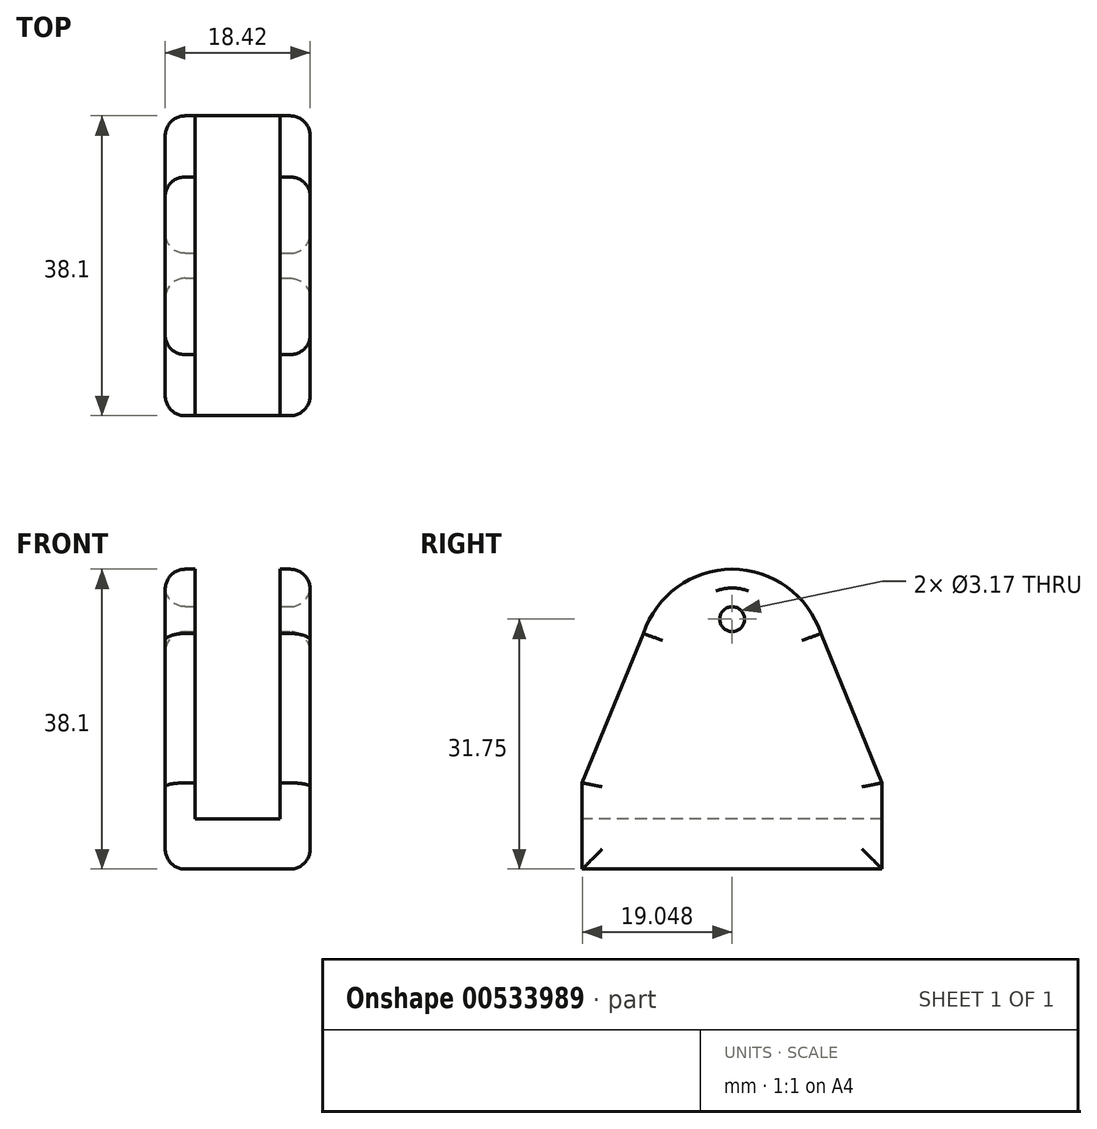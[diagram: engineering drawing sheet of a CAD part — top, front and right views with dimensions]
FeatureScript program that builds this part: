
annotation { "Feature Type Name" : "Feature", "Feature Type Description" : "" }
export const myFeature = defineFeature(function(context is Context, id is Id, definition is map)
    precondition{}
    {
        {
            var Q0;
            Q0=qCreatedBy(makeId("Top.planeOp"),FACE);
            var sketch = newSketch(context, id + "F0", { "sketchPlane" : qUnion([Q0])});
            skLineSegment(sketch, "E0.bottom", {"start": v(0, -20.8) * mm, "end": v(-18.41, -20.8) * mm});
            skLineSegment(sketch, "E0.top", {"start": v(0, -58.9) * mm, "end": v(-18.41, -58.9) * mm});
            skLineSegment(sketch, "E0.left", {"start": v(0, -20.8) * mm, "end": v(0, -58.9) * mm});
            skLineSegment(sketch, "E0.right", {"start": v(-18.42, -20.8) * mm, "end": v(-18.41, -58.9) * mm});
            skSolve(sketch);
        }
        {
            var Q0;
            Q0=makeQuery(id+"F0.imprint","IMPRINT",FACE,{"disambiguationData":[TD([[makeQuery(id+"F0.imprint","IMPRINT",EDGE,{"derivedFrom":sQuery(id+"F0.wireOp",EDGE,"E0.bottom")}),1.0]])]});
            extrude(context, id + "F1", {"entities" : qUnion([Q0]), "depth" : 38.1 * mm, "offsetDistance" : 25.4 * mm});
        }
        {
            var Q0;
            Q0=makeQuery(id+"F1.opExtrude","SWEPT_FACE",FACE,{"disambiguationData":[OSD([sQuery(id+"F0.wireOp",EDGE,"E0.left")])]});
            var sketch = newSketch(context, id + "F2", { "sketchPlane" : qUnion([Q0])});
            skPoint(sketch, "E1.oppositeSnap0", {"position": v(-39.85, 38.1) * mm});
            skLineSegment(sketch, "E1.bottom", {"start": v(-58.9, 0) * mm, "end": v(-39.85, 0) * mm});
            skLineSegment(sketch, "E1.top", {"start": v(-58.9, 31.75) * mm, "end": v(-39.85, 31.75) * mm});
            skLineSegment(sketch, "E1.left", {"start": v(-58.9, 0) * mm, "end": v(-58.9, 31.75) * mm});
            skLineSegment(sketch, "E1.right", {"start": v(-39.85, 0) * mm, "end": v(-39.85, 31.75) * mm});
            skCircle(sketch, "E2", {"center": v(-39.85, 26.24) * mm, "radius": 11.86 * mm});
            skCircle(sketch, "E3", {"center": v(-39.85, 31.75) * mm, "radius": 1.59 * mm});
            skLineSegment(sketch, "E4", {"start": v(-28.58, 29.93) * mm, "end": v(-20.8, 10.96) * mm});
            skLineSegment(sketch, "E5.MirrorCS", {"start": v(-51.12, 29.93) * mm, "end": v(-58.9, 10.96) * mm});
            skSolve(sketch);
        }
        {
            var Q0;
            {var subQ5=sQuery(id+"F2.wireOp",EDGE,"E5.MirrorCS");Q0=makeQuery(id+"F2.imprint","IMPRINT",FACE,{"disambiguationData":[TD([[makeQuery(id+"F2.imprint","IMPRINT",EDGE,{"derivedFrom":subQ5}),-1.0]])]});}
            var Q1;
            {var subQ0=sQuery(id+"F2.wireOp",EDGE,"E1.top");var subQ4=sQuery(id+"F2.wireOp",EDGE,"E2");var subQ5=makeQuery(id+"F2.imprint","INTERSECT",VERTEX,{"derivedFrom":[subQ0,subQ4]});Q1=makeQuery(id+"F2.imprint","IMPRINT",FACE,{"disambiguationData":[TD([[makeQuery(id+"F2.imprint","IMPRINT",EDGE,{"disambiguationData":[TD([[subQ5,1.0]])],"derivedFrom":subQ4}),-1.0]])]});}
            var Q2;
            {var subQ0=sQuery(id+"F2.wireOp",EDGE,"E1.right");var subQ1=sQuery(id+"F2.wireOp",EDGE,"E1.top");var subQ2=makeQuery(id+"F2.imprint","INTERSECT",VERTEX,{"derivedFrom":[subQ1,subQ0]});Q2=makeQuery(id+"F2.imprint","IMPRINT",FACE,{"disambiguationData":[TD([[makeQuery(id+"F2.imprint","IMPRINT",EDGE,{"disambiguationData":[TD([[subQ2,1.0]])],"derivedFrom":subQ1}),1.0]])]});}
            var Q3;
            {var subQ0=sQuery(id+"F2.wireOp",EDGE,"E4");Q3=makeQuery(id+"F2.imprint","IMPRINT",FACE,{"disambiguationData":[TD([[makeQuery(id+"F2.imprint","IMPRINT",EDGE,{"derivedFrom":subQ0}),1.0]])]});}
            var Q4;
            {var subQ0=sQuery(id+"F2.wireOp",EDGE,"E1.right");var subQ1=sQuery(id+"F2.wireOp",EDGE,"E1.top");var subQ2=makeQuery(id+"F2.imprint","INTERSECT",VERTEX,{"derivedFrom":[subQ1,subQ0]});Q4=makeQuery(id+"F2.imprint","IMPRINT",FACE,{"disambiguationData":[TD([[makeQuery(id+"F2.imprint","IMPRINT",EDGE,{"disambiguationData":[TD([[subQ2,1.0]])],"derivedFrom":subQ1}),-1.0]])]});}
            extrude(context, id + "F3", {"entities" : qUnion([Q0, Q1, Q2, Q3, Q4]), "operationType" : NewBodyOperationType.REMOVE, "oppositeDirection" : true, "depth" : 25.4 * mm, "offsetDistance" : 25.4 * mm});
        }
        {
            var Q0;
            Q0=qCreatedBy(makeId("Top.planeOp"),FACE);
            cPlane(context, id + "F4", {"entities" : qUnion([Q0]), "cplaneType" : CPlaneType.OFFSET, "offset" : 38.1 * mm, "width" : 152.4 * mm, "height" : 152.4 * mm});
        }
        {
            var Q0;
            Q0=makeQuery(id+"F1.opExtrude","CAP_FACE",FACE,{"disambiguationData":[OSD([sQuery(id+"F0.wireOp",EDGE,"E0.bottom"),sQuery(id+"F0.wireOp",EDGE,"E0.top"),sQuery(id+"F0.wireOp",EDGE,"E0.left"),sQuery(id+"F0.wireOp",EDGE,"E0.right")])],"isStart":true});
            var sketch = newSketch(context, id + "F5", { "sketchPlane" : qUnion([Q0])});
            skLineSegment(sketch, "E6.bottom", {"start": v(-18.41, 20.8) * mm, "end": v(-14.6, 20.8) * mm});
            skLineSegment(sketch, "E6.top", {"start": v(-18.41, 58.9) * mm, "end": v(-14.6, 58.9) * mm});
            skLineSegment(sketch, "E6.left", {"start": v(-18.41, 20.8) * mm, "end": v(-18.41, 58.9) * mm});
            skLineSegment(sketch, "E6.right", {"start": v(-14.6, 20.8) * mm, "end": v(-14.6, 58.9) * mm});
            skLineSegment(sketch, "E7.bottom", {"start": v(0, 20.8) * mm, "end": v(-3.8, 20.8) * mm});
            skLineSegment(sketch, "E7.top", {"start": v(0, 58.9) * mm, "end": v(-3.81, 58.9) * mm});
            skLineSegment(sketch, "E7.left", {"start": v(0, 20.8) * mm, "end": v(0, 58.9) * mm});
            skLineSegment(sketch, "E7.right", {"start": v(-3.8, 20.8) * mm, "end": v(-3.81, 58.9) * mm});
            skLineSegment(sketch, "E8.bottom", {"start": v(-3.8, 20.8) * mm, "end": v(-14.6, 20.8) * mm});
            skLineSegment(sketch, "E8.top", {"start": v(-3.8, 58.9) * mm, "end": v(-14.6, 58.9) * mm});
            skLineSegment(sketch, "E8.left", {"start": v(-3.8, 20.8) * mm, "end": v(-3.8, 58.9) * mm});
            skSolve(sketch);
        }
        {
            var Q0;
            Q0=makeQuery(id+"F5.imprint","IMPRINT",FACE,{"disambiguationData":[TD([[makeQuery(id+"F5.imprint","IMPRINT",EDGE,{"derivedFrom":sQuery(id+"F5.wireOp",EDGE,"E8.bottom")}),-1.0]])]});
            extrude(context, id + "F6", {"entities" : qUnion([Q0]), "operationType" : NewBodyOperationType.REMOVE, "oppositeDirection" : true, "depth" : 55.12 * mm, "offsetDistance" : 25.4 * mm});
        }
        {
            var Q0;
            {var subQ0=sQuery(id+"F0.wireOp",EDGE,"E0.bottom");var subQ1=sQuery(id+"F0.wireOp",EDGE,"E0.top");var subQ2=sQuery(id+"F0.wireOp",EDGE,"E0.left");Q0=makeQuery(id+"F6.boolean.opBoolean","SPLIT",FACE,{"disambiguationData":[TD([makeQuery(id+"F1.opExtrude","SWEPT_FACE",FACE,{"disambiguationData":[OSD([subQ2])]})])],"derivedFrom":makeQuery(id+"F1.opExtrude","CAP_FACE",FACE,{"disambiguationData":[OSD([subQ0,subQ1,subQ2,sQuery(id+"F0.wireOp",EDGE,"E0.right")])],"isStart":true})});}
            var sketch = newSketch(context, id + "F7", { "sketchPlane" : qUnion([Q0])});
            skLineSegment(sketch, "E9.bottom", {"start": v(0, 20.8) * mm, "end": v(-18.41, 20.8) * mm});
            skLineSegment(sketch, "E9.top", {"start": v(0, 58.9) * mm, "end": v(-18.42, 58.9) * mm});
            skLineSegment(sketch, "E9.left", {"start": v(0, 20.8) * mm, "end": v(0, 58.9) * mm});
            skLineSegment(sketch, "E9.right", {"start": v(-18.41, 20.8) * mm, "end": v(-18.42, 58.9) * mm});
            skSolve(sketch);
        }
        {
            var Q0;
            {var subQ2=sQuery(id+"F7.wireOp",EDGE,"E9.right");Q0=makeQuery(id+"F7.imprint","IMPRINT",FACE,{"disambiguationData":[TD([[makeQuery(id+"F7.imprint","IMPRINT",EDGE,{"derivedFrom":subQ2}),-1.0]])]});}
            extrude(context, id + "F8", {"entities" : qUnion([Q0]), "oppositeDirection" : true, "depth" : 6.35 * mm, "offsetDistance" : 25.4 * mm});
        }
        {
            var Q0;
            Q0=makeQuery(id+"F1.opExtrude","SWEPT_FACE",FACE,{"disambiguationData":[OSD([sQuery(id+"F0.wireOp",EDGE,"E0.left")])]});
            var Q1;
            Q1=makeQuery(id+"F1.opExtrude","SWEPT_FACE",FACE,{"disambiguationData":[OSD([sQuery(id+"F0.wireOp",EDGE,"E0.right")])]});
            fillet(context, id + "F9", {"entities" : qUnion([Q0, Q1]), "radius" : 2.54 * mm, "tangentPropagation" : true, "allowEdgeOverflow" : false});
        }
        {
            var Q0;
            Q0=makeQuery(id+"F6.boolean.opBoolean","SPLIT",BODY,{"disambiguationData":[OD(0.0)],"derivedFrom":makeQuery(id+"F1.opExtrude","SWEPT_BODY",BODY,{"disambiguationData":[OSD([sQuery(id+"F0.wireOp",EDGE,"E0.bottom"),sQuery(id+"F0.wireOp",EDGE,"E0.top"),sQuery(id+"F0.wireOp",EDGE,"E0.left"),sQuery(id+"F0.wireOp",EDGE,"E0.right")])]})});
            var Q1;
            Q1=makeQuery(id+"F6.boolean.opBoolean","SPLIT",BODY,{"disambiguationData":[OD(1.0)],"derivedFrom":makeQuery(id+"F1.opExtrude","SWEPT_BODY",BODY,{"disambiguationData":[OSD([sQuery(id+"F0.wireOp",EDGE,"E0.bottom"),sQuery(id+"F0.wireOp",EDGE,"E0.top"),sQuery(id+"F0.wireOp",EDGE,"E0.left"),sQuery(id+"F0.wireOp",EDGE,"E0.right")])]})});
            var Q2;
            Q2=makeQuery(id+"F8.opExtrude","SWEPT_BODY",BODY,{"disambiguationData":[OSD([sQuery(id+"F5.wireOp",EDGE,"E8.left"),sQuery(id+"F7.wireOp",EDGE,"E9.bottom"),sQuery(id+"F7.wireOp",EDGE,"E9.top"),sQuery(id+"F7.wireOp",EDGE,"E9.right")])]});
            booleanBodies(context, id + "F10", {"operationType" : BooleanOperationType.UNION, "tools" : qUnion([Q0, Q1, Q2])});
        }
        {
            var Q0;
            Q0=makeQuery(id+"F10.opBoolean","MERGE",FACE,{"derivedFrom":[makeQuery(id+"F8.opExtrude","SWEPT_FACE",FACE,{"disambiguationData":[OSD([sQuery(id+"F7.wireOp",EDGE,"E9.right")])]}),makeQuery(id+"F1.opExtrude","SWEPT_FACE",FACE,{"disambiguationData":[OSD([sQuery(id+"F0.wireOp",EDGE,"E0.right")])]})]});
            fillet(context, id + "F11", {"entities" : qUnion([Q0]), "radius" : 2.54 * mm, "tangentPropagation" : true, "allowEdgeOverflow" : false});
        }
    });
